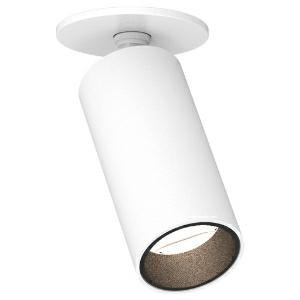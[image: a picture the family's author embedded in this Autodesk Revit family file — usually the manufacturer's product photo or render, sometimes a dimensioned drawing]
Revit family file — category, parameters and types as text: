
# Revit family: imagine_micro_220-1226
name_source: partatom
category: Lighting Fixtures
units: mm (PartAtom-declared; Revit-internal decimal feet)

## family parameters
Cut with Voids When Loaded = No
Host = Face
Light Source = No
Part Type = Normal
Room Calculation Point = No
Round Connector Dimension = Use Diameter
Shared = No

## types (1)
- 220-1226-H27-W22 (1 x LED, 750.48 lm, 8.6 W, 2700K)
    Apparent Load = 9 VA
    CIE Flux Codes = 99 100 100 100 71
    Color Rendering = 1A/90…99
    Color Temperature = 2700K
    Default Elevation = 1800 mm
    Description = IMAGINE MICRO
    Height = 0 mm  [stored 0 ft]
    Lamp = 1 x LED
    Lamp Light Flux = 750.48 lm
    Lamp Power = 8.6 W
    Lamp count = 1
    Length = 35 mm
    Luminous efficacy = 62 lm/W
    Manufacturer = Prolicht
    ModVariant = No
    Model = 220-1226
    Mounting Place = Ceiling
    Mounting Type = Recessed
    Number of Poles = 1
    OnlyDefault = Yes
    Power Factor = 1
    Product Name = IMAGINE MICRO
    Product group = Recessed spotlights
    ProductGroupID = 422
    Protection Class = Protection class
    Protection Degree = Degree of protection
    RLX_Detail_Level = 1
    RlxData = <blob elided: 58037 chars, md5=2dc54cec>
    Socket = socket
    Standby Power = 0 W
    System Light Flux = 529 lm
    System Power = 9 W
    Type Comments = LED COLOUR DIR 2700 K (27),BEAMWIDTH Spot (22)
    Type Image = 220-1226.jpg
    URL = http://relux.com
    VarID = 220-1226-h27-w22
    Voltage = 0 V
    Weight = 0.00 kg
    Width = 0 mm  [stored 0 ft]

note: [stored X ft] marks values corroborated as IEEE doubles in the binary element streams (Revit-internal decimal feet)

## geometry (parser evidence)
native form markers: Blend x4, Sweep x18
no freeform markers — native parametric forms only
